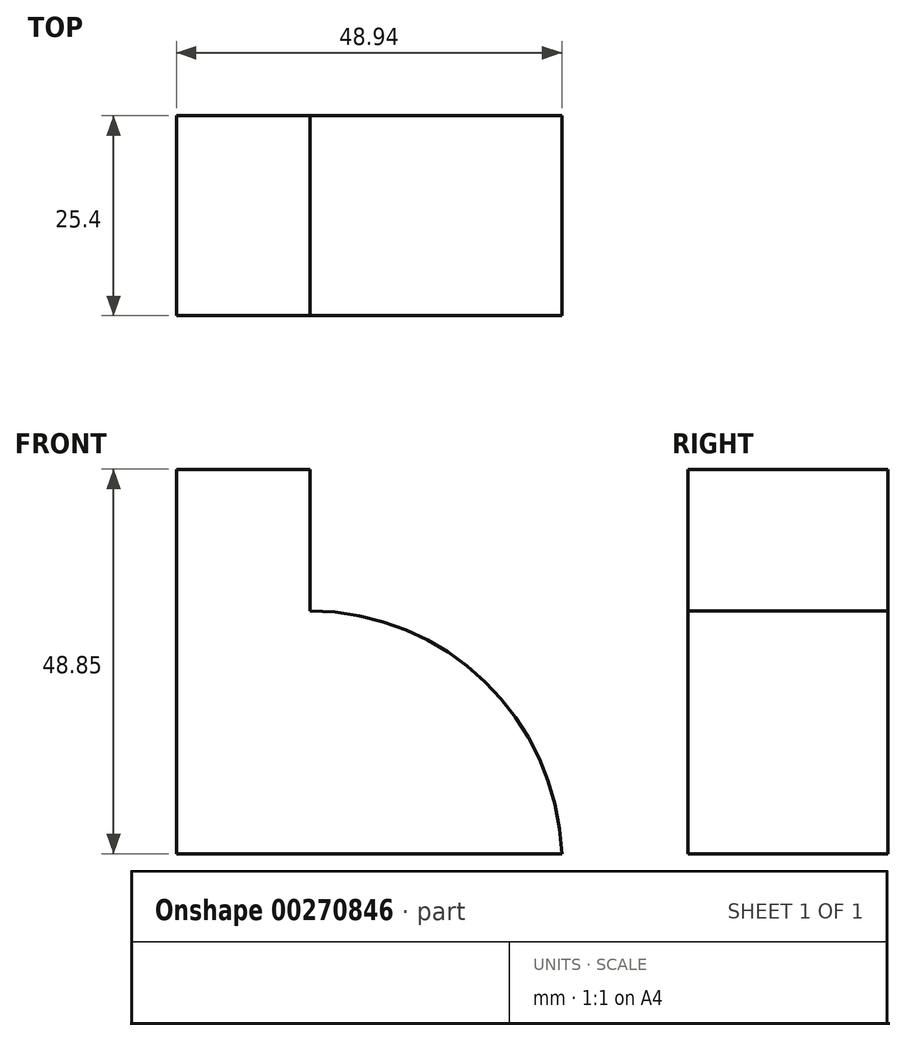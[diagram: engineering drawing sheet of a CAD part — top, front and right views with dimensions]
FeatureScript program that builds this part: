
annotation { "Feature Type Name" : "Feature", "Feature Type Description" : "" }
export const myFeature = defineFeature(function(context is Context, id is Id, definition is map)
    precondition{}
    {
        {
            var Q0;
            Q0=qCreatedBy(makeId("Front.planeOp"),FACE);
            var sketch = newSketch(context, id + "F0", { "sketchPlane" : qUnion([Q0])});
            skLineSegment(sketch, "E0", {"start": v(0, 0) * mm, "end": v(-48.94, 0) * mm});
            skLineSegment(sketch, "E1", {"start": v(-48.94, 0) * mm, "end": v(-48.94, 48.85) * mm});
            skLineSegment(sketch, "E2", {"start": v(-48.94, 48.85) * mm, "end": v(-31.96, 48.85) * mm});
            skLineSegment(sketch, "E3", {"start": v(-31.96, 48.85) * mm, "end": v(-31.96, 30.87) * mm});
            skArc(sketch, "E4", {"start": v(0, 0) * mm, "mid": v(-9.78, 21.85) * mm, "end": v(-31.96, 30.87) * mm});
            skSolve(sketch);
        }
        {
            var Q0;
            Q0 = qSketchRegion(id + "F0", true);
            extrude(context, id + "F1", {"entities" : qUnion([Q0]), "depth" : 25.4 * mm});
        }
    });
